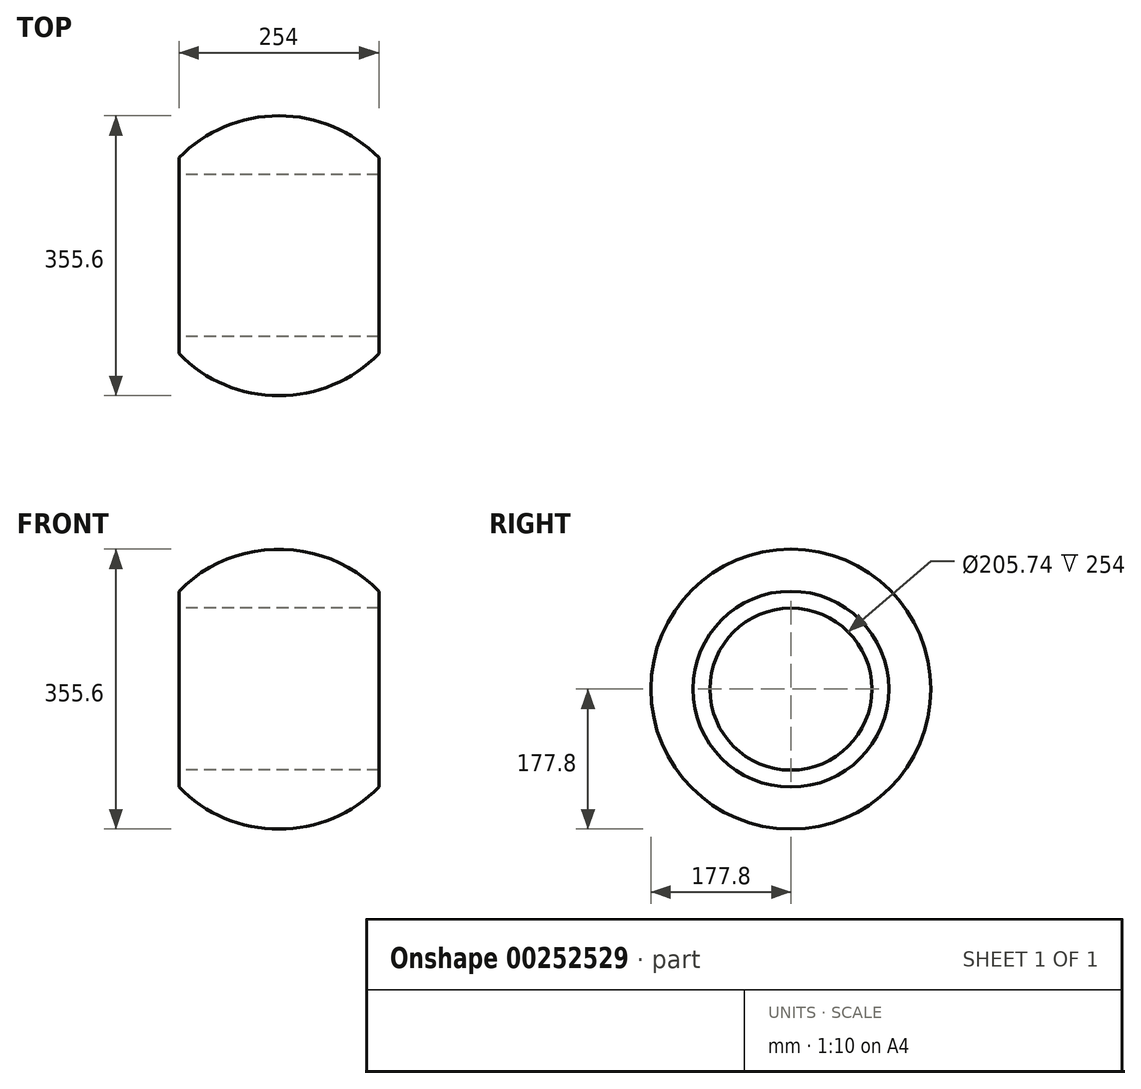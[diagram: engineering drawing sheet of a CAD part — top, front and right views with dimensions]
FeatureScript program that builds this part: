
annotation { "Feature Type Name" : "Feature", "Feature Type Description" : "" }
export const myFeature = defineFeature(function(context is Context, id is Id, definition is map)
    precondition{}
    {
        {
            var Q0;
            Q0=qCreatedBy(makeId("Top.planeOp"),FACE);
            var sketch = newSketch(context, id + "F0", { "sketchPlane" : qUnion([Q0])});
            skArc(sketch, "E0", {"start": v(127, 124.43) * mm, "mid": v(0, 177.8) * mm, "end": v(-127, 124.43) * mm});
            skLineSegment(sketch, "E1", {"start": v(-127, 0) * mm, "end": v(127, 0) * mm});
            skLineSegment(sketch, "E2", {"start": v(-127, 0) * mm, "end": v(-127, 124.43) * mm});
            skLineSegment(sketch, "E3", {"start": v(127, 0) * mm, "end": v(127, 124.43) * mm});
            skPoint(sketch, "E4.orphan", {"position": v(-177.8, 0) * mm});
            skPoint(sketch, "E5.orphan", {"position": v(177.8, 0) * mm});
            skSolve(sketch);
        }
        {
            var Q0;
            Q0=makeQuery(id+"F0.imprint","IMPRINT",FACE,{"disambiguationData":[TD([[makeQuery(id+"F0.imprint","IMPRINT",EDGE,{"derivedFrom":sQuery(id+"F0.wireOp",EDGE,"E0")}),1.0]])]});
            var Q1;
            Q1=sQuery(id+"F0.wireOp",EDGE,"E1");
            revolve(context, id + "F1", {"entities" : qUnion([Q0]), "axis" : qUnion([Q1]), "revolveType" : RevolveType.FULL});
        }
        {
            var Q0;
            Q0=makeQuery(id+"F1.opRevolve","SWEPT_FACE",FACE,{"disambiguationData":[OSD([sQuery(id+"F0.wireOp",EDGE,"E2")])]});
            var sketch = newSketch(context, id + "F2", { "sketchPlane" : qUnion([Q0])});
            skCircle(sketch, "E6", {"center": v(0, 0) * mm, "radius": 102.87 * mm});
            skSolve(sketch);
        }
        {
            var Q0;
            Q0=makeQuery(id+"F2.imprint","IMPRINT",FACE,{"disambiguationData":[TD([[makeQuery(id+"F2.imprint","IMPRINT",EDGE,{"derivedFrom":sQuery(id+"F2.wireOp",EDGE,"E6")}),1.0]])]});
            extrude(context, id + "F3", {"entities" : qUnion([Q0]), "operationType" : NewBodyOperationType.REMOVE, "endBound" : BoundingType.THROUGH_ALL, "oppositeDirection" : true, "depth" : 25.4 * mm});
        }
    });
